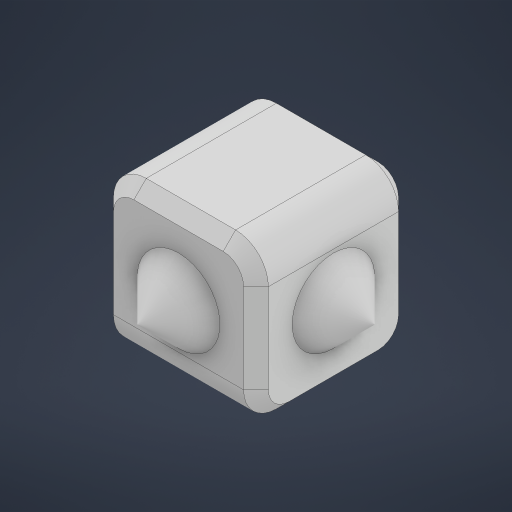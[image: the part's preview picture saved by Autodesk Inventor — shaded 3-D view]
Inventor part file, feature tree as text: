
AUTODESK INVENTOR PART (.ipt)
format: ipt  version: 2024 (Build 280153000, 153)  size: 236,544 bytes
history: native  units: in
note: dims shown in document units (in); Inventor stores cm internally (conversion verified against a paired STEP export)
features: sketch x4, projected_geometry x3, revolve x2, mirror x2, extrude x1, fillet x1, chamfer x1
ambient origin geometry x8: Origin, YZ Plane, XZ Plane, XY Plane, X Axis, Y Axis, Z Axis, Center Point
bodies: Solid1 (feature_tree)
feature tree (14):
  extrude  "Extrusion1"  Depth=0.5906in
  sketch  "Sketch2"  dims[d2=0.5906in d3=0.0in d4=0.315in d5=0.1575in]
  revolve  "Revolution1"  [1 undecoded]
  mirror  "Mirror1"
  fillet  "Fillet1"  Radius=0.1575in
  chamfer  "Chamfer1"  Distance=0.125in Angle=45.0deg
  revolve  "Revolution2"  [1 undecoded]
  mirror  "Mirror2"
  sketch  "Sketch1"  dims[d0=0.5906in d1=0.5906in]
  projected_geometry  "Projected Loop1"
  sketch  "Sketch3"  dims[d6=90.0deg]
  projected_geometry  "Projected Loop2"
  sketch  "Sketch4"  dims[d7=0.125in d8=0.0472in d9=0.125in d10=45.0deg d11=0.1575in d12=0.1575in d13=90.0deg]
  projected_geometry  "Projected Loop3"
note: 2 required parameter values undecoded (feature->parameter linkage not recoverable at this tier; creation-order binding heuristic only, values carry confidence <= 0.55)
